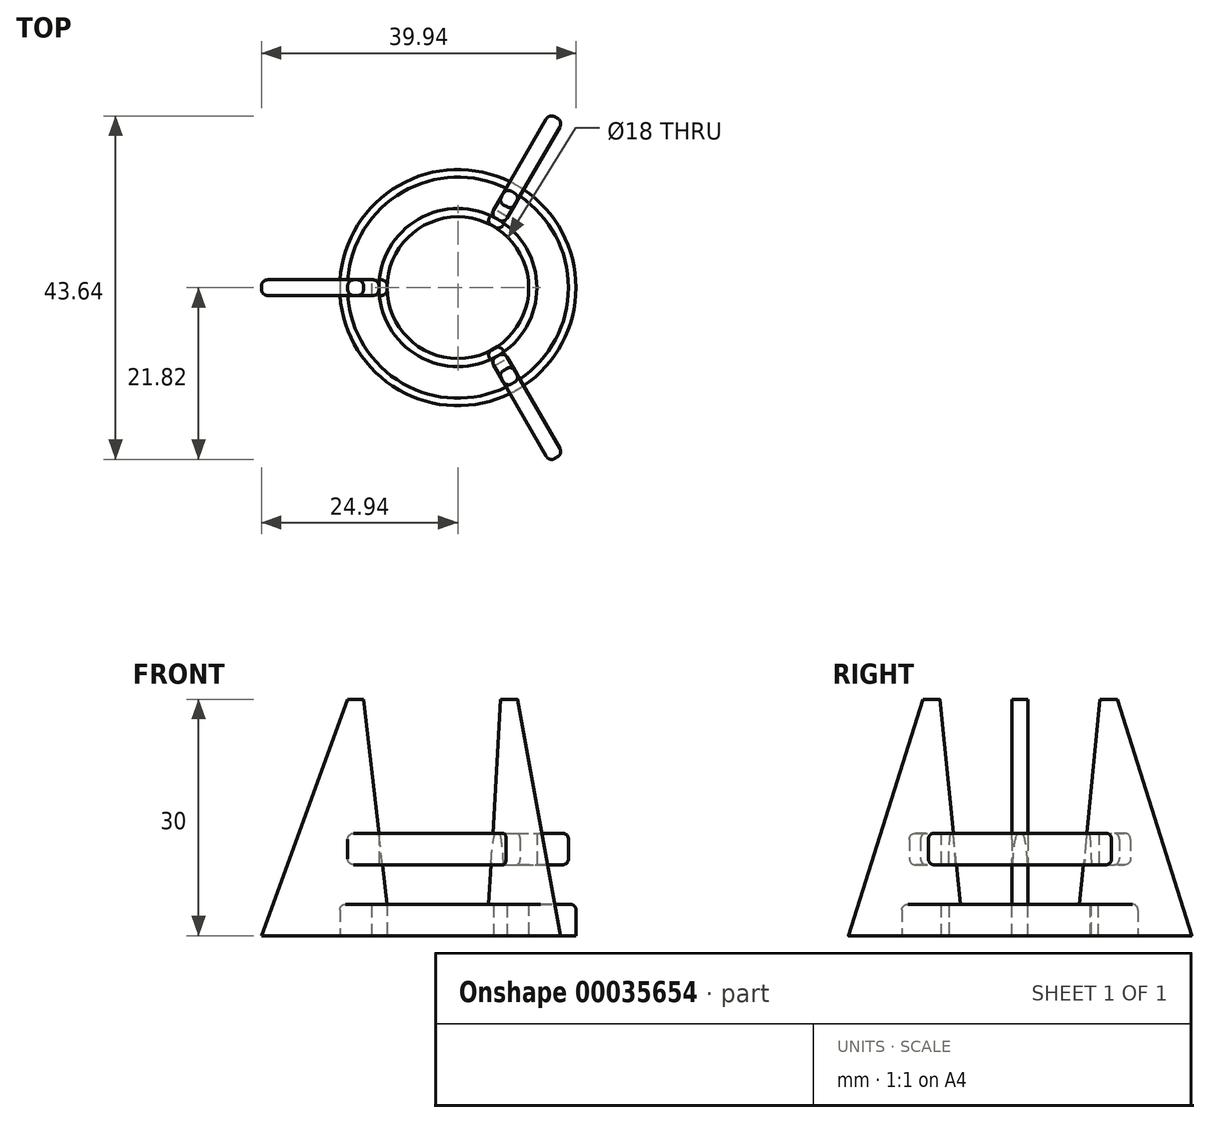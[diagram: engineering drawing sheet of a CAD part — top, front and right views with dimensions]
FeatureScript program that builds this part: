
annotation { "Feature Type Name" : "Feature", "Feature Type Description" : "" }
export const myFeature = defineFeature(function(context is Context, id is Id, definition is map)
    precondition{}
    {
        {
            var Q0;
            Q0=qCreatedBy(makeId("Front.planeOp"),FACE);
            var sketch = newSketch(context, id + "F0", { "sketchPlane" : qUnion([Q0])});
            skLineSegment(sketch, "E0", {"start": v(0, 0) * mm, "end": v(0, 61.45) * mm});
            skSolve(sketch);
        }
        {
            var Q0;
            Q0=qCreatedBy(makeId("Front.planeOp"),FACE);
            var sketch = newSketch(context, id + "F1", { "sketchPlane" : qUnion([Q0])});
            skLineSegment(sketch, "E1.bottom", {"start": v(-15, 0) * mm, "end": v(-9, 0) * mm});
            skLineSegment(sketch, "E1.top", {"start": v(-15, 4) * mm, "end": v(-9, 4) * mm});
            skLineSegment(sketch, "E1.left", {"start": v(-15, 0) * mm, "end": v(-15, 4) * mm});
            skLineSegment(sketch, "E1.right", {"start": v(-9, 0) * mm, "end": v(-9, 4) * mm});
            skSolve(sketch);
        }
        {
            var Q0;
            Q0 = qSketchRegion(id + "F1", true);
            var Q1;
            Q1=sQuery(id+"F0.wireOp",EDGE,"E0");
            revolve(context, id + "F2", {"entities" : qUnion([Q0]), "axis" : qUnion([Q1]), "revolveType" : RevolveType.FULL});
        }
        {
            var Q0;
            Q0=qCreatedBy(makeId("Front.planeOp"),FACE);
            var sketch = newSketch(context, id + "F3", { "sketchPlane" : qUnion([Q0])});
            skLineSegment(sketch, "E2", {"start": v(-9, 4) * mm, "end": v(-12, 30) * mm});
            skLineSegment(sketch, "E3", {"start": v(-12, 30) * mm, "end": v(-14, 30) * mm});
            skLineSegment(sketch, "E4", {"start": v(-14, 30) * mm, "end": v(-24.94, 0) * mm});
            skLineSegment(sketch, "E5", {"start": v(-24.94, 0) * mm, "end": v(-10.93, 0) * mm});
            skLineSegment(sketch, "E6", {"start": v(-10.93, 0) * mm, "end": v(-10.93, 4) * mm});
            skLineSegment(sketch, "E7", {"start": v(-10.93, 4) * mm, "end": v(-9, 4) * mm});
            skSolve(sketch);
        }
        {
            var Q0;
            Q0 = qSketchRegion(id + "F3", true);
            extrude(context, id + "F4", {"entities" : qUnion([Q0]), "depth" : 2 * mm, "symmetric" : true});
        }
        {
            var Q0;
            Q0=makeQuery(id+"F4.opExtrude","SWEPT_BODY",BODY,{"disambiguationData":[OSD([sQuery(id+"F3.wireOp",EDGE,"E2"),sQuery(id+"F3.wireOp",EDGE,"E3"),sQuery(id+"F3.wireOp",EDGE,"E4"),sQuery(id+"F3.wireOp",EDGE,"E5"),sQuery(id+"F3.wireOp",EDGE,"E6"),sQuery(id+"F3.wireOp",EDGE,"E7")])]});
            var Q1;
            Q1=qCreatedBy(makeId("Right.planeOp"),FACE);
            mirror(context, id + "F5", {"entities" : qUnion([Q0]), "mirrorPlane" : qUnion([Q1])});
        }
        {
            var Q0;
            Q0=makeQuery(id+"F5.opPattern","COPY",BODY,{"derivedFrom":makeQuery(id+"F4.opExtrude","SWEPT_BODY",BODY,{"disambiguationData":[OSD([sQuery(id+"F3.wireOp",EDGE,"E2"),sQuery(id+"F3.wireOp",EDGE,"E3"),sQuery(id+"F3.wireOp",EDGE,"E4"),sQuery(id+"F3.wireOp",EDGE,"E5"),sQuery(id+"F3.wireOp",EDGE,"E6"),sQuery(id+"F3.wireOp",EDGE,"E7")])]}),"instanceName":"1"});
            var Q1;
            Q1=sQuery(id+"F0.wireOp",EDGE,"E0");
            transform(context, id + "F6", {"entities" : qUnion([Q0]), "transformType" : TransformType.ROTATION, "transformAxis" : qUnion([Q1]), "angle" : 60 * degree, "makeCopy" : false});
        }
        {
            var Q0;
            Q0=makeQuery(id+"F4.opExtrude","SWEPT_BODY",BODY,{"disambiguationData":[OSD([sQuery(id+"F3.wireOp",EDGE,"E2"),sQuery(id+"F3.wireOp",EDGE,"E3"),sQuery(id+"F3.wireOp",EDGE,"E4"),sQuery(id+"F3.wireOp",EDGE,"E5"),sQuery(id+"F3.wireOp",EDGE,"E6"),sQuery(id+"F3.wireOp",EDGE,"E7")])]});
            var Q1;
            Q1=qCreatedBy(makeId("Right.planeOp"),FACE);
            mirror(context, id + "F7", {"entities" : qUnion([Q0]), "mirrorPlane" : qUnion([Q1])});
        }
        {
            var Q0;
            Q0=makeQuery(id+"F7.opPattern","COPY",BODY,{"derivedFrom":makeQuery(id+"F4.opExtrude","SWEPT_BODY",BODY,{"disambiguationData":[OSD([sQuery(id+"F3.wireOp",EDGE,"E2"),sQuery(id+"F3.wireOp",EDGE,"E3"),sQuery(id+"F3.wireOp",EDGE,"E4"),sQuery(id+"F3.wireOp",EDGE,"E5"),sQuery(id+"F3.wireOp",EDGE,"E6"),sQuery(id+"F3.wireOp",EDGE,"E7")])]}),"instanceName":"1"});
            var Q1;
            Q1=sQuery(id+"F0.wireOp",EDGE,"E0");
            transform(context, id + "F8", {"entities" : qUnion([Q0]), "transformType" : TransformType.ROTATION, "transformAxis" : qUnion([Q1]), "angle" : 60 * degree, "oppositeDirection" : true, "makeCopy" : false});
        }
        {
            var Q0;
            Q0=qCreatedBy(makeId("Front.planeOp"),FACE);
            var sketch = newSketch(context, id + "F9", { "sketchPlane" : qUnion([Q0])});
            skLineSegment(sketch, "E8.bottom", {"start": v(-10.04, 13) * mm, "end": v(-14.04, 13) * mm});
            skLineSegment(sketch, "E8.top", {"start": v(-10.04, 9) * mm, "end": v(-14.04, 9) * mm});
            skLineSegment(sketch, "E8.left", {"start": v(-10.04, 13) * mm, "end": v(-10.04, 9) * mm});
            skLineSegment(sketch, "E8.right", {"start": v(-14.04, 13) * mm, "end": v(-14.04, 9) * mm});
            skSolve(sketch);
        }
        {
            var Q0;
            Q0 = qSketchRegion(id + "F9", true);
            var Q1;
            Q1=sQuery(id+"F0.wireOp",EDGE,"E0");
            revolve(context, id + "F10", {"operationType" : NewBodyOperationType.ADD, "surfaceOperationType" : NewSurfaceOperationType.NEW, "entities" : qUnion([Q0]), "axis" : qUnion([Q1]), "revolveType" : RevolveType.FULL});
        }
        {
            var Q0;
            Q0=makeQuery(id+"F10.opRevolve","SWEPT_EDGE",EDGE,{"disambiguationData":[OSD([sQuery(id+"F9.wireOp",EDGE,"E8.top"),sQuery(id+"F9.wireOp",EDGE,"E8.right")])]});
            var Q1;
            Q1=makeQuery(id+"F10.opRevolve","SWEPT_EDGE",EDGE,{"disambiguationData":[OSD([sQuery(id+"F9.wireOp",EDGE,"E8.bottom"),sQuery(id+"F9.wireOp",EDGE,"E8.right")])]});
            var Q2;
            Q2=makeQuery(id+"F2.opRevolve","SWEPT_EDGE",EDGE,{"disambiguationData":[OSD([sQuery(id+"F1.wireOp",EDGE,"E1.top"),sQuery(id+"F1.wireOp",EDGE,"E1.left")])]});
            fillet(context, id + "F11", {"entities" : qUnion([Q0, Q1, Q2]), "radius" : 0.75 * mm, "tangentPropagation" : true, "allowEdgeOverflow" : false});
        }
        {
            var Q0;
            Q0=makeQuery(id+"F7.opPattern","COPY",EDGE,{"derivedFrom":makeQuery(id+"F4.opExtrude","CAP_EDGE",EDGE,{"disambiguationData":[OSD([sQuery(id+"F3.wireOp",EDGE,"E4")])],"isStart":false}),"instanceName":"1"});
            var Q1;
            Q1=makeQuery(id+"F7.opPattern","COPY",EDGE,{"derivedFrom":makeQuery(id+"F4.opExtrude","CAP_EDGE",EDGE,{"disambiguationData":[OSD([sQuery(id+"F3.wireOp",EDGE,"E4")])],"isStart":true}),"instanceName":"1"});
            var Q2;
            Q2=makeQuery(id+"F4.opExtrude","CAP_EDGE",EDGE,{"disambiguationData":[OSD([sQuery(id+"F3.wireOp",EDGE,"E4")])],"isStart":false});
            var Q3;
            Q3=makeQuery(id+"F4.opExtrude","CAP_EDGE",EDGE,{"disambiguationData":[OSD([sQuery(id+"F3.wireOp",EDGE,"E4")])],"isStart":true});
            var Q4;
            Q4=makeQuery(id+"F5.opPattern","COPY",EDGE,{"derivedFrom":makeQuery(id+"F4.opExtrude","CAP_EDGE",EDGE,{"disambiguationData":[OSD([sQuery(id+"F3.wireOp",EDGE,"E4")])],"isStart":true}),"instanceName":"1"});
            var Q5;
            Q5=makeQuery(id+"F5.opPattern","COPY",EDGE,{"derivedFrom":makeQuery(id+"F4.opExtrude","CAP_EDGE",EDGE,{"disambiguationData":[OSD([sQuery(id+"F3.wireOp",EDGE,"E4")])],"isStart":false}),"instanceName":"1"});
            fillet(context, id + "F12", {"entities" : qUnion([Q0, Q1, Q2, Q3, Q4, Q5]), "radius" : 0.75 * mm, "tangentPropagation" : true, "allowEdgeOverflow" : false});
        }
        {
            var Q0;
            Q0=makeQuery(id+"F7.opPattern","COPY",EDGE,{"derivedFrom":makeQuery(id+"F4.opExtrude","CAP_EDGE",EDGE,{"disambiguationData":[OSD([sQuery(id+"F3.wireOp",EDGE,"E2")])],"isStart":true}),"instanceName":"1"});
            var Q1;
            Q1=makeQuery(id+"F7.opPattern","COPY",EDGE,{"derivedFrom":makeQuery(id+"F4.opExtrude","CAP_EDGE",EDGE,{"disambiguationData":[OSD([sQuery(id+"F3.wireOp",EDGE,"E2")])],"isStart":false}),"instanceName":"1"});
            var Q2;
            Q2=makeQuery(id+"F5.opPattern","COPY",EDGE,{"derivedFrom":makeQuery(id+"F4.opExtrude","CAP_EDGE",EDGE,{"disambiguationData":[OSD([sQuery(id+"F3.wireOp",EDGE,"E2")])],"isStart":false}),"instanceName":"1"});
            var Q3;
            Q3=makeQuery(id+"F5.opPattern","COPY",EDGE,{"derivedFrom":makeQuery(id+"F4.opExtrude","CAP_EDGE",EDGE,{"disambiguationData":[OSD([sQuery(id+"F3.wireOp",EDGE,"E2")])],"isStart":true}),"instanceName":"1"});
            var Q4;
            Q4=makeQuery(id+"F4.opExtrude","CAP_EDGE",EDGE,{"disambiguationData":[OSD([sQuery(id+"F3.wireOp",EDGE,"E2")])],"isStart":true});
            var Q5;
            Q5=makeQuery(id+"F4.opExtrude","CAP_EDGE",EDGE,{"disambiguationData":[OSD([sQuery(id+"F3.wireOp",EDGE,"E2")])],"isStart":false});
            fillet(context, id + "F13", {"entities" : qUnion([Q0, Q1, Q2, Q3, Q4, Q5]), "radius" : 0.75 * mm, "tangentPropagation" : true, "allowEdgeOverflow" : false});
        }
    });
